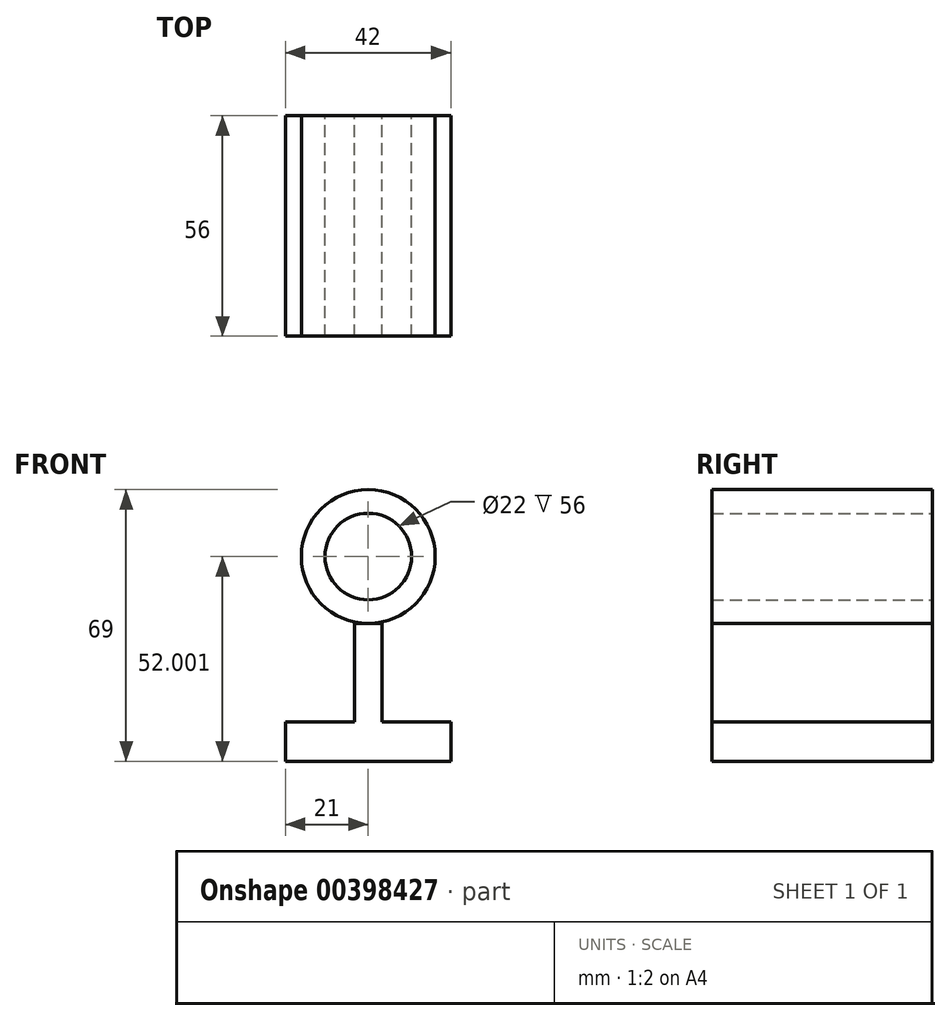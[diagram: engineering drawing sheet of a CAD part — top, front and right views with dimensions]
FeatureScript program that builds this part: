
annotation { "Feature Type Name" : "Feature", "Feature Type Description" : "" }
export const myFeature = defineFeature(function(context is Context, id is Id, definition is map)
    precondition{}
    {
        {
            var Q0;
            Q0=qCreatedBy(makeId("Front.planeOp"),FACE);
            var sketch = newSketch(context, id + "F0", { "sketchPlane" : qUnion([Q0])});
            skCircle(sketch, "E0", {"center": v(0, 43.34) * mm, "radius": 17 * mm});
            skCircle(sketch, "E1", {"center": v(0, 43.34) * mm, "radius": 11 * mm});
            skLineSegment(sketch, "E2.bottom", {"start": v(-3.5, 26.34) * mm, "end": v(3.5, 26.34) * mm});
            skLineSegment(sketch, "E2.top", {"start": v(-3.5, 1.34) * mm, "end": v(3.5, 1.34) * mm});
            skLineSegment(sketch, "E2.left", {"start": v(-3.5, 26.34) * mm, "end": v(-3.5, 1.34) * mm});
            skLineSegment(sketch, "E2.right", {"start": v(3.5, 26.34) * mm, "end": v(3.5, 1.34) * mm});
            skLineSegment(sketch, "E3.bottom", {"start": v(-21, 1.34) * mm, "end": v(21, 1.34) * mm});
            skLineSegment(sketch, "E3.top", {"start": v(-21, -8.66) * mm, "end": v(21, -8.66) * mm});
            skLineSegment(sketch, "E3.left", {"start": v(-21, 1.34) * mm, "end": v(-21, -8.66) * mm});
            skLineSegment(sketch, "E3.right", {"start": v(21, 1.34) * mm, "end": v(21, -8.66) * mm});
            skSolve(sketch);
        }
        {
            var Q0;
            Q0 = qSketchRegion(id + "F0", true);
            extrude(context, id + "F1", {"entities" : qUnion([Q0]), "depth" : 56 * mm});
        }
        {
            var Q0;
            Q0=qCreatedBy(makeId("Front.planeOp"),FACE);
            var sketch = newSketch(context, id + "F2", { "sketchPlane" : qUnion([Q0])});
            skLineSegment(sketch, "E4.bottom", {"start": v(-6, -13.78) * mm, "end": v(6, -13.78) * mm});
            skLineSegment(sketch, "E4.top", {"start": v(-6, -3.78) * mm, "end": v(6, -3.78) * mm});
            skLineSegment(sketch, "E4.left", {"start": v(-6, -13.78) * mm, "end": v(-6, -3.78) * mm});
            skLineSegment(sketch, "E4.right", {"start": v(6, -13.78) * mm, "end": v(6, -3.78) * mm});
            skPoint(sketch, "E4.middle", {"position": v(0, -8.78) * mm});
            skSolve(sketch);
        }
        {
            var Q0;
            Q0 = qSketchRegion(id + "F2", true);
            extrude(context, id + "F3", {"entities" : qUnion([Q0]), "operationType" : NewBodyOperationType.REMOVE, "oppositeDirection" : true, "depth" : 70 * mm});
        }
    });
